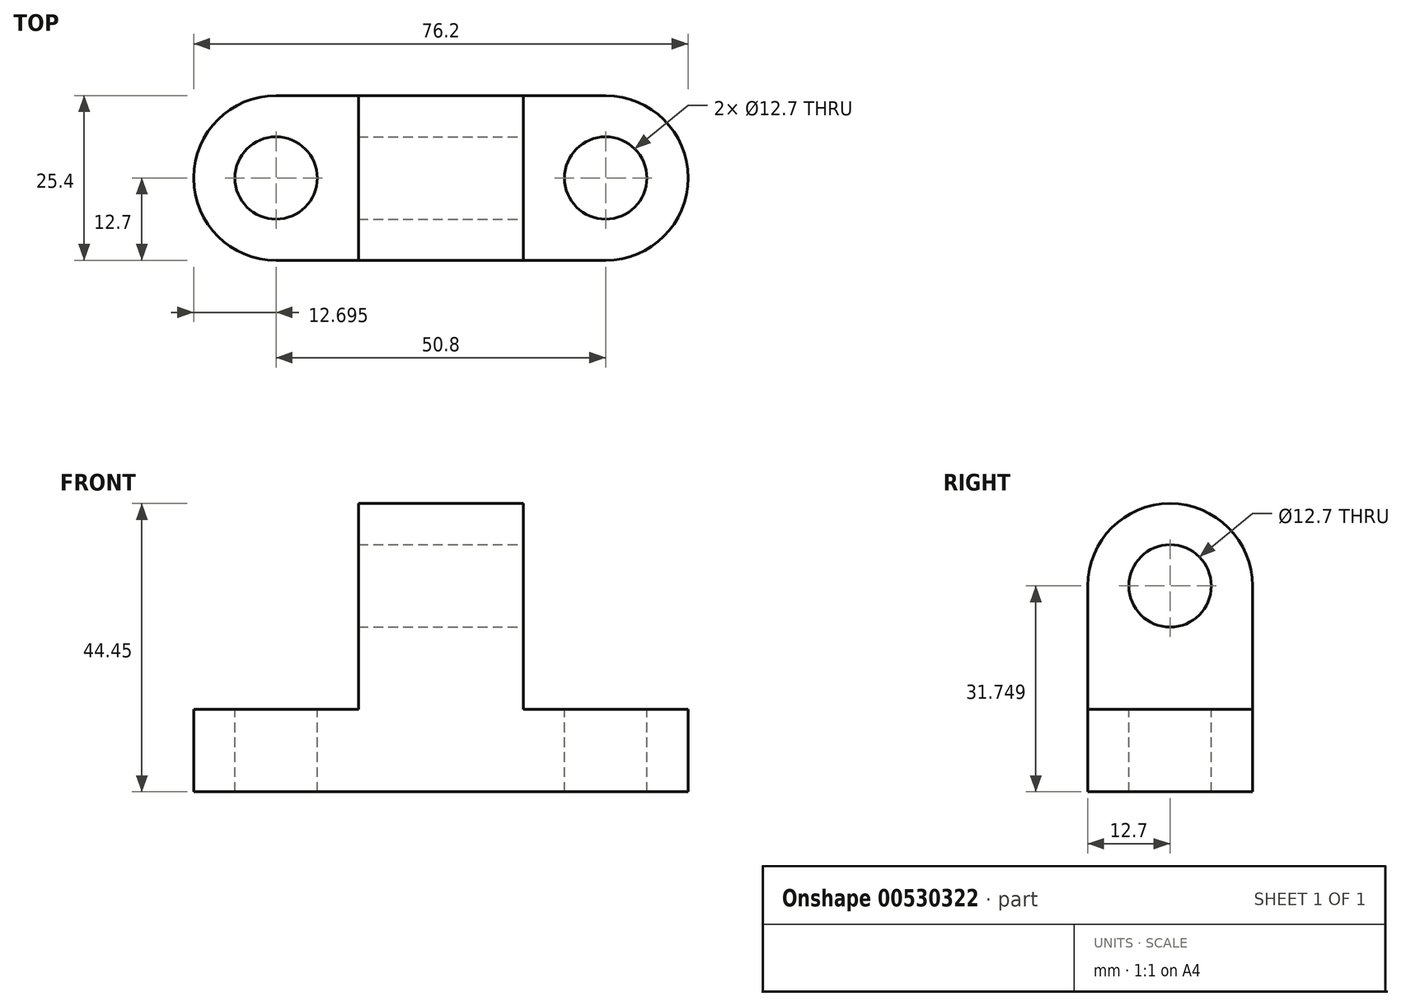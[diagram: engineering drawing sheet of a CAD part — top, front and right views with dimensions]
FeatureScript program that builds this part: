
annotation { "Feature Type Name" : "Feature", "Feature Type Description" : "" }
export const myFeature = defineFeature(function(context is Context, id is Id, definition is map)
    precondition{}
    {
        {
            var Q0;
            Q0=qCreatedBy(makeId("Front.planeOp"),FACE);
            var sketch = newSketch(context, id + "F0", { "sketchPlane" : qUnion([Q0])});
            skLineSegment(sketch, "E0", {"start": v(-70.57, 5.73) * mm, "end": v(5.63, 5.73) * mm});
            skLineSegment(sketch, "E1", {"start": v(5.63, 5.73) * mm, "end": v(5.63, 18.43) * mm});
            skLineSegment(sketch, "E2", {"start": v(5.63, 18.43) * mm, "end": v(-19.77, 18.43) * mm});
            skLineSegment(sketch, "E3", {"start": v(-19.77, 18.43) * mm, "end": v(-19.77, 50.18) * mm});
            skLineSegment(sketch, "E4", {"start": v(-19.77, 50.18) * mm, "end": v(-45.17, 50.18) * mm});
            skLineSegment(sketch, "E5", {"start": v(-70.57, 5.73) * mm, "end": v(-70.57, 18.43) * mm});
            skLineSegment(sketch, "E6", {"start": v(-70.57, 18.43) * mm, "end": v(-45.17, 18.43) * mm});
            skLineSegment(sketch, "E7", {"start": v(-45.17, 18.43) * mm, "end": v(-45.17, 50.18) * mm});
            skSolve(sketch);
        }
        {
            var Q0;
            Q0=makeQuery(id+"F0.imprint","IMPRINT",FACE,{"disambiguationData":[TD([[makeQuery(id+"F0.imprint","IMPRINT",EDGE,{"derivedFrom":sQuery(id+"F0.wireOp",EDGE,"E0")}),1.0]])]});
            extrude(context, id + "F1", {"entities" : qUnion([Q0]), "depth" : 25.4 * mm, "offsetDistance" : 25.4 * mm});
        }
        {
            var Q0;
            Q0=makeQuery(id+"F1.opExtrude","SWEPT_FACE",FACE,{"disambiguationData":[OSD([sQuery(id+"F0.wireOp",EDGE,"E2")])]});
            var sketch = newSketch(context, id + "F2", { "sketchPlane" : qUnion([Q0])});
            skCircle(sketch, "E8", {"center": v(-7.07, -12.7) * mm, "radius": 6.35 * mm});
            skArc(sketch, "E9", {"start": v(-7.07, -25.4) * mm, "mid": v(5.63, -12.7) * mm, "end": v(-7.07, 0) * mm});
            skSolve(sketch);
        }
        {
            var Q0;
            Q0=makeQuery(id+"F2.imprint","IMPRINT",FACE,{"disambiguationData":[TD([[makeQuery(id+"F2.imprint","IMPRINT",EDGE,{"derivedFrom":sQuery(id+"F2.wireOp",EDGE,"E8")}),1.0]])]});
            var Q1;
            {var subQ0=sQuery(id+"F2.wireOp",EDGE,"E9");var subQ1=sQuery(id+"F0.wireOp",EDGE,"E2");var subQ2=makeQuery(id+"F1.opExtrude","CAP_EDGE",EDGE,{"disambiguationData":[OSD([subQ1])],"isStart":false});var subQ3=makeQuery(id+"F2.imprint","INTERSECT",VERTEX,{"derivedFrom":[subQ2,subQ0]});Q1=makeQuery(id+"F2.imprint","IMPRINT",FACE,{"disambiguationData":[TD([[makeQuery(id+"F2.imprint","IMPRINT",EDGE,{"disambiguationData":[TD([[subQ3,-1.0]])],"derivedFrom":subQ0}),-1.0]])]});}
            var Q2;
            {var subQ0=sQuery(id+"F2.wireOp",EDGE,"E9");var subQ1=sQuery(id+"F0.wireOp",EDGE,"E2");var subQ2=makeQuery(id+"F1.opExtrude","CAP_EDGE",EDGE,{"disambiguationData":[OSD([subQ1])],"isStart":true});var subQ3=makeQuery(id+"F2.imprint","INTERSECT",VERTEX,{"derivedFrom":[subQ2,subQ0]});Q2=makeQuery(id+"F2.imprint","IMPRINT",FACE,{"disambiguationData":[TD([[makeQuery(id+"F2.imprint","IMPRINT",EDGE,{"disambiguationData":[TD([[subQ3,1.0]])],"derivedFrom":subQ0}),-1.0]])]});}
            extrude(context, id + "F3", {"entities" : qUnion([Q0, Q1, Q2]), "operationType" : NewBodyOperationType.REMOVE, "endBound" : BoundingType.THROUGH_ALL, "oppositeDirection" : true, "depth" : 25.4 * mm, "offsetDistance" : 25.4 * mm});
        }
        {
            var Q0;
            Q0=makeQuery(id+"F1.opExtrude","SWEPT_FACE",FACE,{"disambiguationData":[OSD([sQuery(id+"F0.wireOp",EDGE,"E3")])]});
            var sketch = newSketch(context, id + "F4", { "sketchPlane" : qUnion([Q0])});
            skCircle(sketch, "E10", {"center": v(-12.7, 37.48) * mm, "radius": 6.35 * mm});
            skLineSegment(sketch, "E11", {"start": v(-19.05, 37.48) * mm, "end": v(-25.4, 37.48) * mm});
            skLineSegment(sketch, "E12", {"start": v(-6.35, 37.48) * mm, "end": v(0, 37.48) * mm});
            skLineSegment(sketch, "E13", {"start": v(-12.7, 43.83) * mm, "end": v(-12.7, 50.18) * mm});
            skArc(sketch, "E14", {"start": v(0, 37.48) * mm, "mid": v(-12.7, 50.18) * mm, "end": v(-25.4, 37.48) * mm});
            skSolve(sketch);
        }
        {
            var Q0;
            {var subQ0=sQuery(id+"F4.wireOp",EDGE,"E10");var subQ1=makeQuery(id+"F4.imprint","INTERSECT",VERTEX,{"derivedFrom":[subQ0,sQuery(id+"F4.wireOp",EDGE,"E12")]});Q0=makeQuery(id+"F4.imprint","IMPRINT",FACE,{"disambiguationData":[TD([[makeQuery(id+"F4.imprint","IMPRINT",EDGE,{"disambiguationData":[TD([[subQ1,-1.0]])],"derivedFrom":subQ0}),1.0]])]});}
            var Q1;
            {var subQ1=sQuery(id+"F0.wireOp",EDGE,"E3");var subQ2=makeQuery(id+"F1.opExtrude","CAP_EDGE",EDGE,{"disambiguationData":[OSD([subQ1])],"isStart":false});var subQ4=makeQuery(id+"F1.opExtrude","SWEPT_EDGE",EDGE,{"disambiguationData":[OSD([subQ1,sQuery(id+"F0.wireOp",EDGE,"E4")])]});var subQ6=makeQuery(id+"F4.imprint","INTERSECT",VERTEX,{"derivedFrom":[subQ4,subQ2]});Q1=makeQuery(id+"F4.imprint","IMPRINT",FACE,{"disambiguationData":[TD([[makeQuery(id+"F4.imprint","IMPRINT",EDGE,{"disambiguationData":[TD([[subQ6,1.0]])],"derivedFrom":subQ2}),-1.0]])]});}
            var Q2;
            {var subQ1=sQuery(id+"F0.wireOp",EDGE,"E3");var subQ2=makeQuery(id+"F1.opExtrude","CAP_EDGE",EDGE,{"disambiguationData":[OSD([subQ1])],"isStart":true});var subQ4=makeQuery(id+"F1.opExtrude","SWEPT_EDGE",EDGE,{"disambiguationData":[OSD([subQ1,sQuery(id+"F0.wireOp",EDGE,"E4")])]});var subQ6=makeQuery(id+"F4.imprint","INTERSECT",VERTEX,{"derivedFrom":[subQ4,subQ2]});Q2=makeQuery(id+"F4.imprint","IMPRINT",FACE,{"disambiguationData":[TD([[makeQuery(id+"F4.imprint","IMPRINT",EDGE,{"disambiguationData":[TD([[subQ6,1.0]])],"derivedFrom":subQ2}),1.0]])]});}
            extrude(context, id + "F5", {"entities" : qUnion([Q0, Q1, Q2]), "operationType" : NewBodyOperationType.REMOVE, "endBound" : BoundingType.THROUGH_ALL, "oppositeDirection" : true, "depth" : 25.4 * mm, "offsetDistance" : 25.4 * mm});
        }
        {
            var Q0;
            Q0=makeQuery(id+"F1.opExtrude","SWEPT_FACE",FACE,{"disambiguationData":[OSD([sQuery(id+"F0.wireOp",EDGE,"E6")])]});
            var sketch = newSketch(context, id + "F6", { "sketchPlane" : qUnion([Q0])});
            skCircle(sketch, "E15", {"center": v(-57.87, -12.7) * mm, "radius": 6.35 * mm});
            skLineSegment(sketch, "E16", {"start": v(-57.87, -6.35) * mm, "end": v(-57.87, 0) * mm});
            skLineSegment(sketch, "E17", {"start": v(-57.87, -19.05) * mm, "end": v(-57.87, -25.4) * mm});
            skLineSegment(sketch, "E18", {"start": v(-64.22, -12.7) * mm, "end": v(-70.57, -12.8) * mm});
            skArc(sketch, "E19", {"start": v(-57.87, 0) * mm, "mid": v(-70.58, -12.7) * mm, "end": v(-57.87, -25.4) * mm});
            skSolve(sketch);
        }
        {
            var Q0;
            {var subQ0=sQuery(id+"F6.wireOp",EDGE,"E19");var subQ1=sQuery(id+"F0.wireOp",EDGE,"E6");var subQ4=makeQuery(id+"F1.opExtrude","SWEPT_EDGE",EDGE,{"disambiguationData":[OSD([sQuery(id+"F0.wireOp",EDGE,"E5"),subQ1])]});var subQ5=makeQuery(id+"F6.imprint","INTERSECT",VERTEX,{"derivedFrom":[subQ4,subQ0]});Q0=makeQuery(id+"F6.imprint","IMPRINT",FACE,{"disambiguationData":[TD([[makeQuery(id+"F6.imprint","IMPRINT",EDGE,{"disambiguationData":[TD([[subQ5,1.0]])],"derivedFrom":subQ0}),-1.0]])]});}
            var Q1;
            {var subQ0=sQuery(id+"F6.wireOp",EDGE,"E19");var subQ1=sQuery(id+"F0.wireOp",EDGE,"E6");var subQ4=makeQuery(id+"F1.opExtrude","CAP_EDGE",EDGE,{"disambiguationData":[OSD([subQ1])],"isStart":false});var subQ5=makeQuery(id+"F6.imprint","INTERSECT",VERTEX,{"derivedFrom":[subQ4,subQ0]});Q1=makeQuery(id+"F6.imprint","IMPRINT",FACE,{"disambiguationData":[TD([[makeQuery(id+"F6.imprint","IMPRINT",EDGE,{"disambiguationData":[TD([[subQ5,1.0]])],"derivedFrom":subQ4}),1.0]])]});}
            var Q2;
            {var subQ0=sQuery(id+"F6.wireOp",EDGE,"E15");var subQ1=makeQuery(id+"F6.imprint","INTERSECT",VERTEX,{"derivedFrom":[subQ0,sQuery(id+"F6.wireOp",EDGE,"E16")]});Q2=makeQuery(id+"F6.imprint","IMPRINT",FACE,{"disambiguationData":[TD([[makeQuery(id+"F6.imprint","IMPRINT",EDGE,{"disambiguationData":[TD([[subQ1,-1.0]])],"derivedFrom":subQ0}),1.0]])]});}
            extrude(context, id + "F7", {"entities" : qUnion([Q0, Q1, Q2]), "operationType" : NewBodyOperationType.REMOVE, "endBound" : BoundingType.THROUGH_ALL, "oppositeDirection" : true, "depth" : 25.4 * mm, "offsetDistance" : 25.4 * mm});
        }
    });
